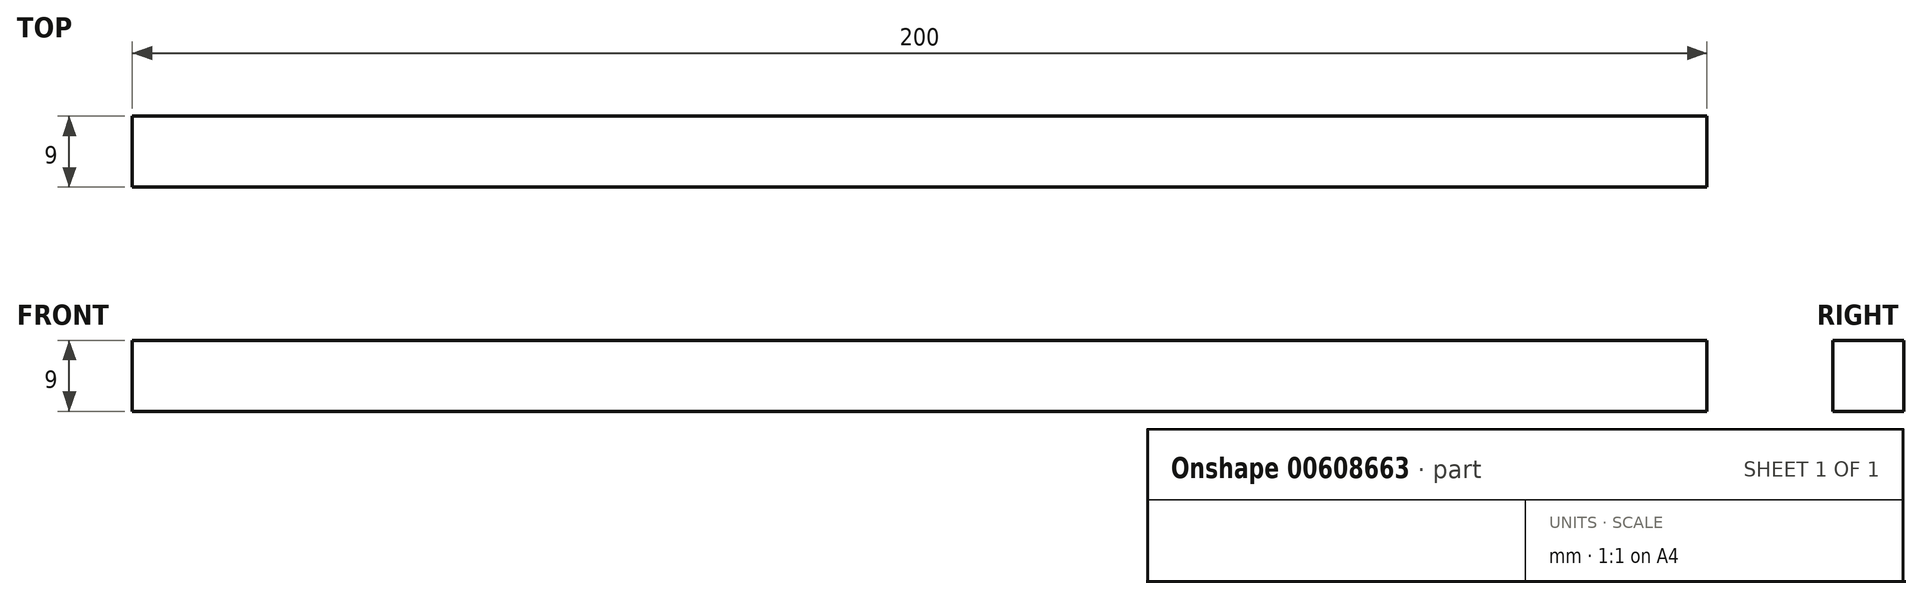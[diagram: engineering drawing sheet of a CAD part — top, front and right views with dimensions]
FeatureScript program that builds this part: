
annotation { "Feature Type Name" : "Feature", "Feature Type Description" : "" }
export const myFeature = defineFeature(function(context is Context, id is Id, definition is map)
    precondition{}
    {
        {
            var Q0;
            Q0=qCreatedBy(makeId("Front.planeOp"),FACE);
            var sketch = newSketch(context, id + "F0", { "sketchPlane" : qUnion([Q0])});
            skLineSegment(sketch, "E0.bottom", {"start": v(100, -4.5) * mm, "end": v(-100, -4.5) * mm});
            skLineSegment(sketch, "E0.top", {"start": v(100, 4.5) * mm, "end": v(-100, 4.5) * mm});
            skLineSegment(sketch, "E0.left", {"start": v(100, -4.5) * mm, "end": v(100, 4.5) * mm});
            skLineSegment(sketch, "E0.right", {"start": v(-100, -4.5) * mm, "end": v(-100, 4.5) * mm});
            skPoint(sketch, "E0.middle", {"position": v(0, 0) * mm});
            skSolve(sketch);
        }
        {
            var Q0;
            Q0=makeQuery(id+"F0.imprint","IMPRINT",FACE,{"disambiguationData":[TD([[makeQuery(id+"F0.imprint","IMPRINT",EDGE,{"derivedFrom":sQuery(id+"F0.wireOp",EDGE,"E0.bottom")}),-1.0]])]});
            extrude(context, id + "F1", {"entities" : qUnion([Q0]), "depth" : 9 * mm, "offsetDistance" : 25 * mm});
        }
    });
